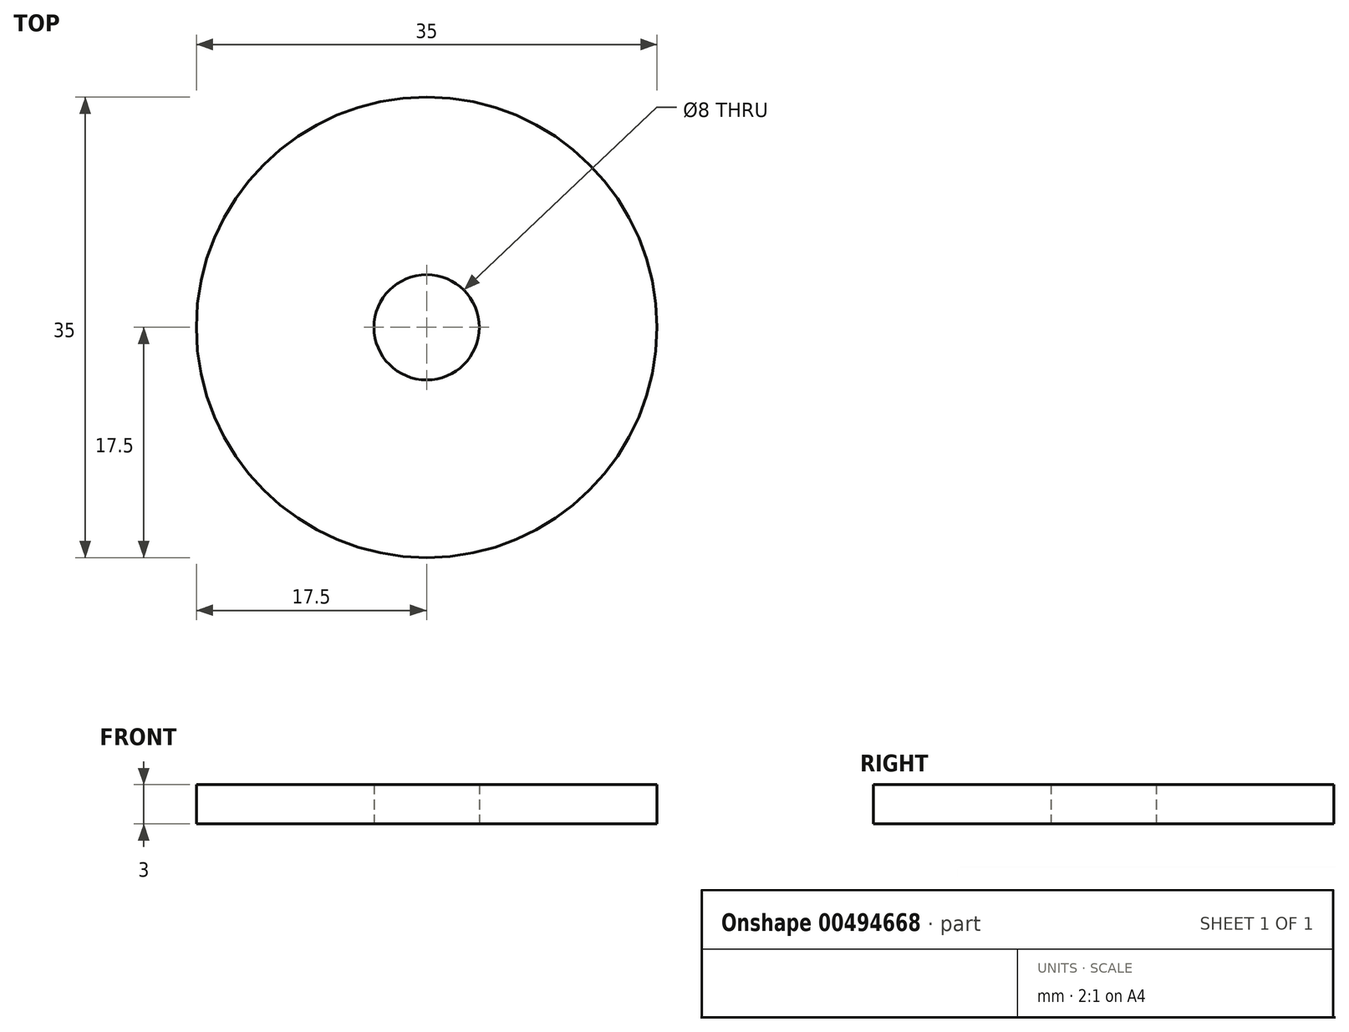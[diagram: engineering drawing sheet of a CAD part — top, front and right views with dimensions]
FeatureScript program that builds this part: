
annotation { "Feature Type Name" : "Feature", "Feature Type Description" : "" }
export const myFeature = defineFeature(function(context is Context, id is Id, definition is map)
    precondition{}
    {
        {
            var Q0;
            Q0=qCreatedBy(makeId("Top.planeOp"),FACE);
            var sketch = newSketch(context, id + "F0", { "sketchPlane" : qUnion([Q0])});
            skCircle(sketch, "E0", {"center": v(0, 0) * mm, "radius": 4 * mm});
            skCircle(sketch, "E1", {"center": v(0, 0) * mm, "radius": 17.5 * mm});
            skSolve(sketch);
        }
        {
            var Q0;
            Q0=makeQuery(id+"F0.imprint","IMPRINT",FACE,{"disambiguationData":[TD([[makeQuery(id+"F0.imprint","IMPRINT",EDGE,{"derivedFrom":sQuery(id+"F0.wireOp",EDGE,"E0")}),-1.0]])]});
            extrude(context, id + "F1", {"entities" : qUnion([Q0]), "depth" : 3 * mm});
        }
    });
